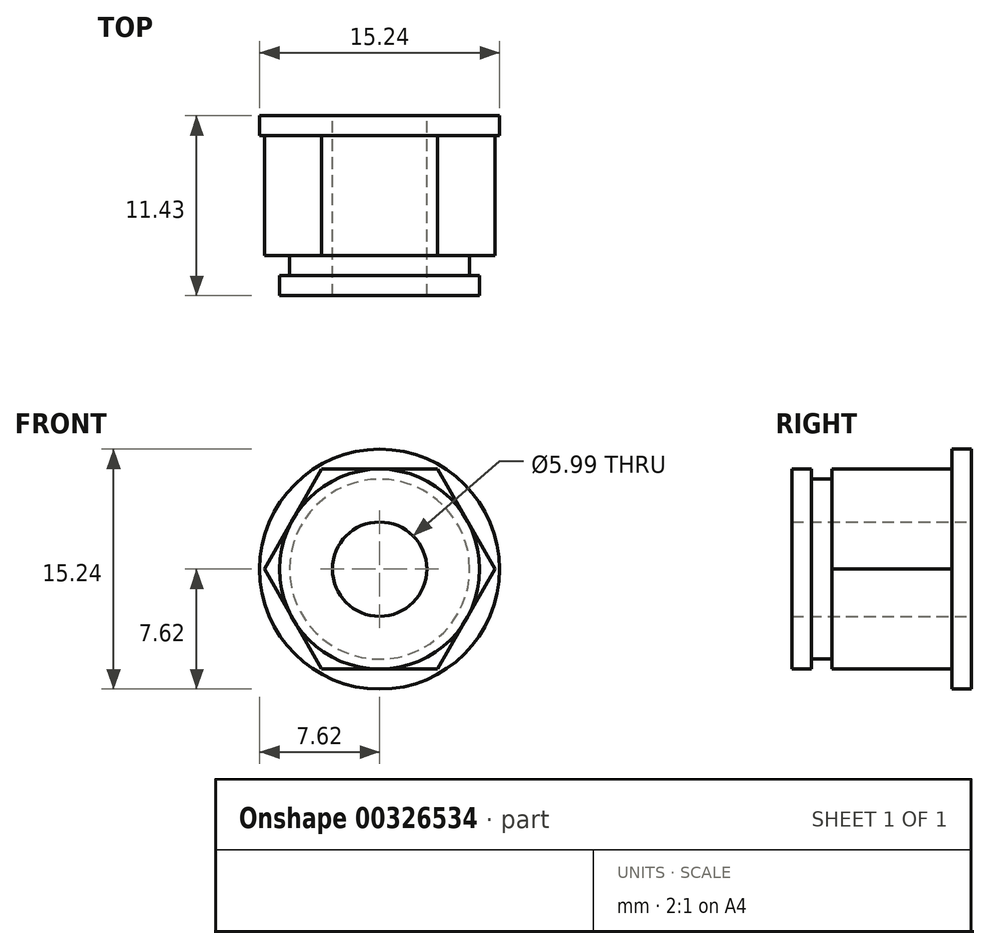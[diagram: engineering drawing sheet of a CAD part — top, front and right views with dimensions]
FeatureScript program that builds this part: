
annotation { "Feature Type Name" : "Feature", "Feature Type Description" : "" }
export const myFeature = defineFeature(function(context is Context, id is Id, definition is map)
    precondition{}
    {
        {
            var Q0;
            Q0=qCreatedBy(makeId("Front.planeOp"),FACE);
            var sketch = newSketch(context, id + "F0", { "sketchPlane" : qUnion([Q0])});
            skLineSegment(sketch, "E0", {"start": v(0, 54.83) * mm, "end": v(0, -52.62) * mm});
            skLineSegment(sketch, "E1", {"start": v(-43.96, 0) * mm, "end": v(47.64, 0) * mm});
            skLineSegment(sketch, "E2", {"start": v(0, 6.35) * mm, "end": v(-3.68, 6.35) * mm});
            skLineSegment(sketch, "E3", {"start": v(-3.68, 6.35) * mm, "end": v(-7.32, 0) * mm});
            skLineSegment(sketch, "E4.MirrorCS", {"start": v(0, -6.35) * mm, "end": v(-3.68, -6.35) * mm});
            skLineSegment(sketch, "E5.MirrorCS", {"start": v(-3.68, -6.35) * mm, "end": v(-7.32, 0) * mm});
            skLineSegment(sketch, "E6.MirrorCS", {"start": v(3.68, -6.35) * mm, "end": v(7.32, 0) * mm});
            skLineSegment(sketch, "E7.MirrorCS", {"start": v(3.68, 6.35) * mm, "end": v(7.32, 0) * mm});
            skLineSegment(sketch, "E8.MirrorCS", {"start": v(0, -6.35) * mm, "end": v(3.68, -6.35) * mm});
            skLineSegment(sketch, "E9.MirrorCS", {"start": v(0, 6.35) * mm, "end": v(3.68, 6.35) * mm});
            skCircle(sketch, "E10", {"center": v(0, 0) * mm, "radius": 7.62 * mm});
            skCircle(sketch, "E11", {"center": v(0, 0) * mm, "radius": 3 * mm});
            skSolve(sketch);
        }
        {
            var Q0;
            Q0 = qSketchRegion(id + "F0", true);
            extrude(context, id + "F1", {"entities" : qUnion([Q0]), "depth" : 1.27 * mm});
        }
        {
            var Q0;
            {var subQ1=sQuery(id+"F0.wireOp",EDGE,"E7.MirrorCS");Q0=makeQuery(id+"F0.imprint","IMPRINT",FACE,{"disambiguationData":[TD([[makeQuery(id+"F0.imprint","IMPRINT",EDGE,{"derivedFrom":subQ1}),-1.0]])]});}
            var Q1;
            {var subQ1=sQuery(id+"F0.wireOp",EDGE,"E2");Q1=makeQuery(id+"F0.imprint","IMPRINT",FACE,{"disambiguationData":[TD([[makeQuery(id+"F0.imprint","IMPRINT",EDGE,{"derivedFrom":subQ1}),1.0]])]});}
            var Q2;
            {var subQ1=sQuery(id+"F0.wireOp",EDGE,"E4.MirrorCS");Q2=makeQuery(id+"F0.imprint","IMPRINT",FACE,{"disambiguationData":[TD([[makeQuery(id+"F0.imprint","IMPRINT",EDGE,{"derivedFrom":subQ1}),-1.0]])]});}
            var Q3;
            {var subQ1=sQuery(id+"F0.wireOp",EDGE,"E6.MirrorCS");Q3=makeQuery(id+"F0.imprint","IMPRINT",FACE,{"disambiguationData":[TD([[makeQuery(id+"F0.imprint","IMPRINT",EDGE,{"derivedFrom":subQ1}),1.0]])]});}
            extrude(context, id + "F2", {"entities" : qUnion([Q0, Q1, Q2, Q3]), "operationType" : NewBodyOperationType.ADD, "depth" : 8.9 * mm});
        }
        {
            var Q0;
            Q0=makeQuery(id+"F2.opExtrude","CAP_FACE",FACE,{"disambiguationData":[OSD([sQuery(id+"F0.wireOp",EDGE,"E2"),sQuery(id+"F0.wireOp",EDGE,"E3"),sQuery(id+"F0.wireOp",EDGE,"E4.MirrorCS"),sQuery(id+"F0.wireOp",EDGE,"E5.MirrorCS"),sQuery(id+"F0.wireOp",EDGE,"E6.MirrorCS"),sQuery(id+"F0.wireOp",EDGE,"E7.MirrorCS"),sQuery(id+"F0.wireOp",EDGE,"E8.MirrorCS"),sQuery(id+"F0.wireOp",EDGE,"E9.MirrorCS"),sQuery(id+"F0.wireOp",EDGE,"E11")])],"isStart":false});
            var sketch = newSketch(context, id + "F3", { "sketchPlane" : qUnion([Q0])});
            skCircle(sketch, "E12", {"center": v(0, 0) * mm, "radius": 5.72 * mm});
            skCircle(sketch, "E13", {"center": v(0, 0) * mm, "radius": 3 * mm});
            skSolve(sketch);
        }
        {
            var Q0;
            Q0 = qSketchRegion(id + "F3", true);
            extrude(context, id + "F4", {"entities" : qUnion([Q0]), "operationType" : NewBodyOperationType.ADD, "depth" : 1.27 * mm});
        }
        {
            var Q0;
            Q0=makeQuery(id+"F4.opExtrude","CAP_FACE",FACE,{"disambiguationData":[OSD([sQuery(id+"F3.wireOp",EDGE,"E12"),sQuery(id+"F3.wireOp",EDGE,"E13")])],"isStart":false});
            var sketch = newSketch(context, id + "F5", { "sketchPlane" : qUnion([Q0])});
            skCircle(sketch, "E14", {"center": v(0, 0) * mm, "radius": 3 * mm});
            skCircle(sketch, "E15", {"center": v(0, 0) * mm, "radius": 6.35 * mm});
            skSolve(sketch);
        }
        {
            var Q0;
            Q0 = qSketchRegion(id + "F5", true);
            extrude(context, id + "F6", {"entities" : qUnion([Q0]), "operationType" : NewBodyOperationType.ADD, "depth" : 1.27 * mm});
        }
    });
